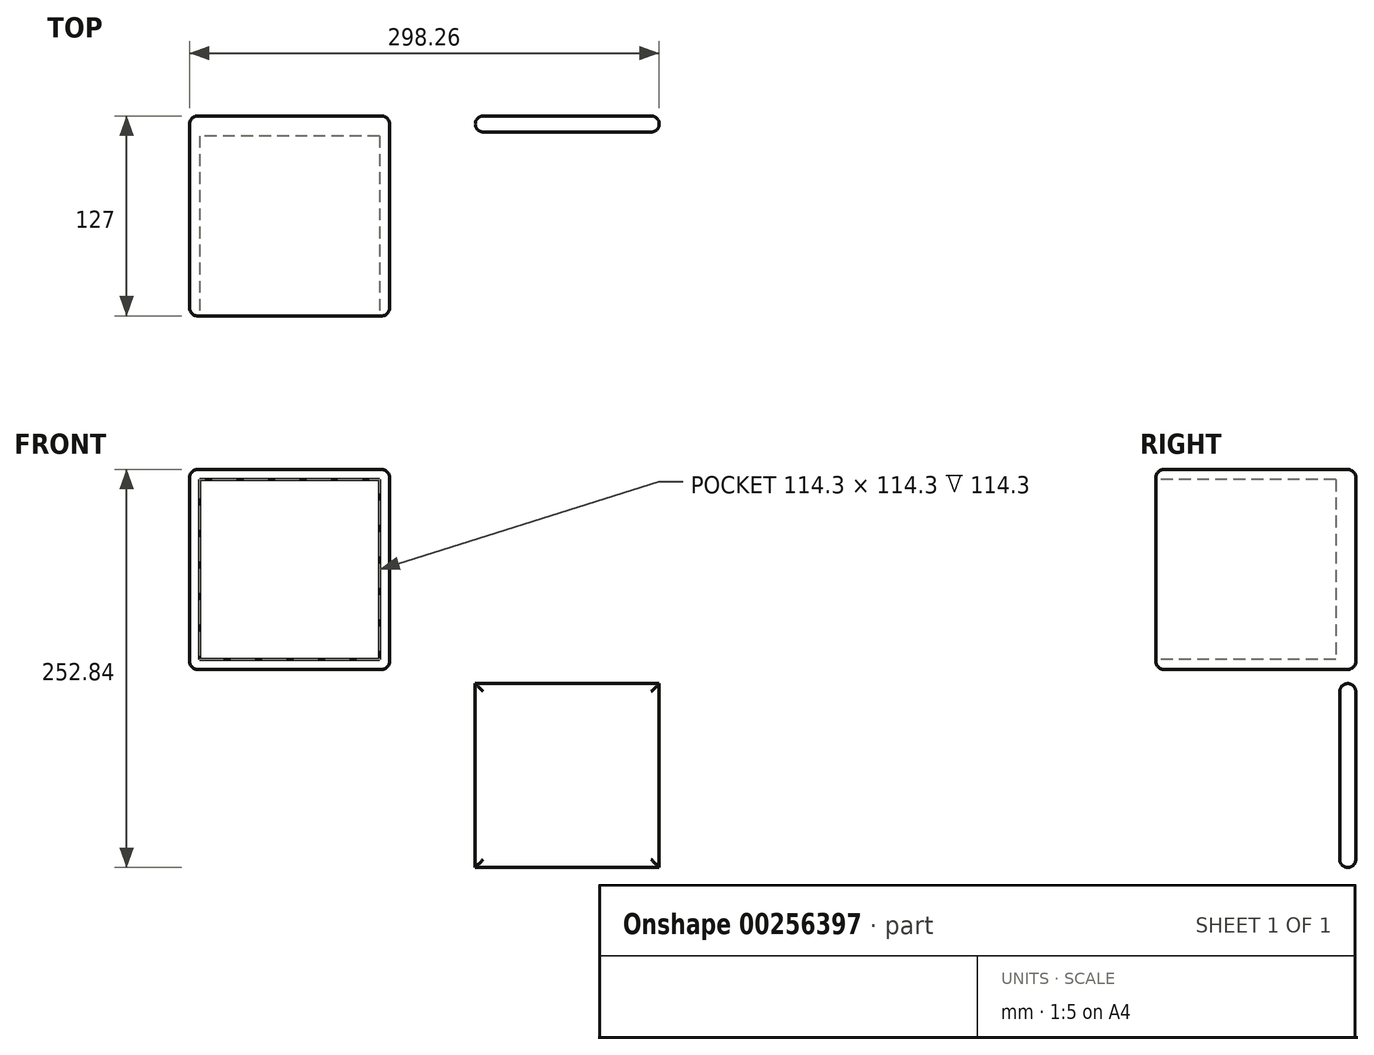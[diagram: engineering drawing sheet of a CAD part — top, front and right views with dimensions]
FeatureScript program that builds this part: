
annotation { "Feature Type Name" : "Feature", "Feature Type Description" : "" }
export const myFeature = defineFeature(function(context is Context, id is Id, definition is map)
    precondition{}
    {
        {
            var Q0;
            Q0=qCreatedBy(makeId("Front.planeOp"),FACE);
            var sketch = newSketch(context, id + "F0", { "sketchPlane" : qUnion([Q0])});
            skLineSegment(sketch, "E0.bottom", {"start": v(-3.08, -9.77) * mm, "end": v(-130.08, -9.77) * mm});
            skLineSegment(sketch, "E0.top", {"start": v(-3.08, 117.23) * mm, "end": v(-130.08, 117.23) * mm});
            skLineSegment(sketch, "E0.left", {"start": v(-3.08, -9.77) * mm, "end": v(-3.08, 117.23) * mm});
            skLineSegment(sketch, "E0.right", {"start": v(-130.08, -9.77) * mm, "end": v(-130.08, 117.23) * mm});
            skPoint(sketch, "E0.middle", {"position": v(-66.58, 53.73) * mm});
            skLineSegment(sketch, "E1.bottom", {"start": v(51.34, -18.77) * mm, "end": v(168.18, -18.77) * mm});
            skLineSegment(sketch, "E1.top", {"start": v(51.34, -135.6) * mm, "end": v(168.18, -135.6) * mm});
            skLineSegment(sketch, "E1.left", {"start": v(51.34, -18.77) * mm, "end": v(51.34, -135.6) * mm});
            skLineSegment(sketch, "E1.right", {"start": v(168.18, -18.77) * mm, "end": v(168.18, -135.6) * mm});
            skPoint(sketch, "E1.middle", {"position": v(109.76, -77.19) * mm});
            skSolve(sketch);
        }
        {
            var Q0;
            Q0=makeQuery(id+"F0.imprint","IMPRINT",FACE,{"disambiguationData":[TD([[makeQuery(id+"F0.imprint","IMPRINT",EDGE,{"derivedFrom":sQuery(id+"F0.wireOp",EDGE,"E0.bottom")}),-1.0]])]});
            extrude(context, id + "F1", {"entities" : qUnion([Q0]), "depth" : 127 * mm});
        }
        {
            var Q0;
            Q0=makeQuery(id+"F0.imprint","IMPRINT",FACE,{"disambiguationData":[TD([[makeQuery(id+"F0.imprint","IMPRINT",EDGE,{"derivedFrom":sQuery(id+"F0.wireOp",EDGE,"E1.bottom")}),-1.0]])]});
            extrude(context, id + "F2", {"entities" : qUnion([Q0]), "depth" : 10.16 * mm});
        }
        {
            var Q0;
            Q0=makeQuery(id+"F2.opExtrude","CAP_FACE",FACE,{"disambiguationData":[OSD([sQuery(id+"F0.wireOp",EDGE,"E1.bottom"),sQuery(id+"F0.wireOp",EDGE,"E1.top"),sQuery(id+"F0.wireOp",EDGE,"E1.left"),sQuery(id+"F0.wireOp",EDGE,"E1.right")])],"isStart":false});
            fillet(context, id + "F3", {"entities" : qUnion([Q0]), "radius" : 5.08 * mm, "tangentPropagation" : true, "allowEdgeOverflow" : false});
        }
        {
            var Q0;
            Q0=makeQuery(id+"F1.opExtrude","CAP_FACE",FACE,{"disambiguationData":[OSD([sQuery(id+"F0.wireOp",EDGE,"E0.bottom"),sQuery(id+"F0.wireOp",EDGE,"E0.top"),sQuery(id+"F0.wireOp",EDGE,"E0.left"),sQuery(id+"F0.wireOp",EDGE,"E0.right")])],"isStart":false});
            var sketch = newSketch(context, id + "F4", { "sketchPlane" : qUnion([Q0])});
            skPoint(sketch, "E2.middle", {"position": v(-66.58, 53.73) * mm});
            skLineSegment(sketch, "E3.bottom", {"start": v(-9.43, 110.88) * mm, "end": v(-123.73, 110.88) * mm});
            skLineSegment(sketch, "E3.top", {"start": v(-9.43, -3.42) * mm, "end": v(-123.73, -3.42) * mm});
            skLineSegment(sketch, "E3.left", {"start": v(-9.43, 110.88) * mm, "end": v(-9.43, -3.42) * mm});
            skLineSegment(sketch, "E3.right", {"start": v(-123.73, 110.88) * mm, "end": v(-123.73, -3.42) * mm});
            skSolve(sketch);
        }
        {
            var Q0;
            Q0=makeQuery(id+"F4.imprint","IMPRINT",FACE,{"disambiguationData":[TD([[makeQuery(id+"F4.imprint","IMPRINT",EDGE,{"derivedFrom":sQuery(id+"F4.wireOp",EDGE,"E3.bottom")}),1.0]])]});
            extrude(context, id + "F5", {"entities" : qUnion([Q0]), "operationType" : NewBodyOperationType.REMOVE, "oppositeDirection" : true, "depth" : 114.3 * mm});
        }
        {
            var Q0;
            Q0=makeQuery(id+"F1.opExtrude","SWEPT_FACE",FACE,{"disambiguationData":[OSD([sQuery(id+"F0.wireOp",EDGE,"E0.bottom")])]});
            var Q1;
            Q1=makeQuery(id+"F1.opExtrude","SWEPT_FACE",FACE,{"disambiguationData":[OSD([sQuery(id+"F0.wireOp",EDGE,"E0.right")])]});
            var Q2;
            Q2=makeQuery(id+"F1.opExtrude","SWEPT_FACE",FACE,{"disambiguationData":[OSD([sQuery(id+"F0.wireOp",EDGE,"E0.left")])]});
            var Q3;
            Q3=makeQuery(id+"F1.opExtrude","SWEPT_FACE",FACE,{"disambiguationData":[OSD([sQuery(id+"F0.wireOp",EDGE,"E0.top")])]});
            fillet(context, id + "F6", {"entities" : qUnion([Q0, Q1, Q2, Q3]), "radius" : 5.08 * mm, "tangentPropagation" : true, "allowEdgeOverflow" : false});
        }
        {
            var Q0;
            Q0=makeQuery(id+"F2.opExtrude","CAP_FACE",FACE,{"disambiguationData":[OSD([sQuery(id+"F0.wireOp",EDGE,"E1.bottom"),sQuery(id+"F0.wireOp",EDGE,"E1.top"),sQuery(id+"F0.wireOp",EDGE,"E1.left"),sQuery(id+"F0.wireOp",EDGE,"E1.right")])],"isStart":true});
            fillet(context, id + "F7", {"entities" : qUnion([Q0]), "radius" : 5.08 * mm, "tangentPropagation" : true, "allowEdgeOverflow" : false});
        }
    });
